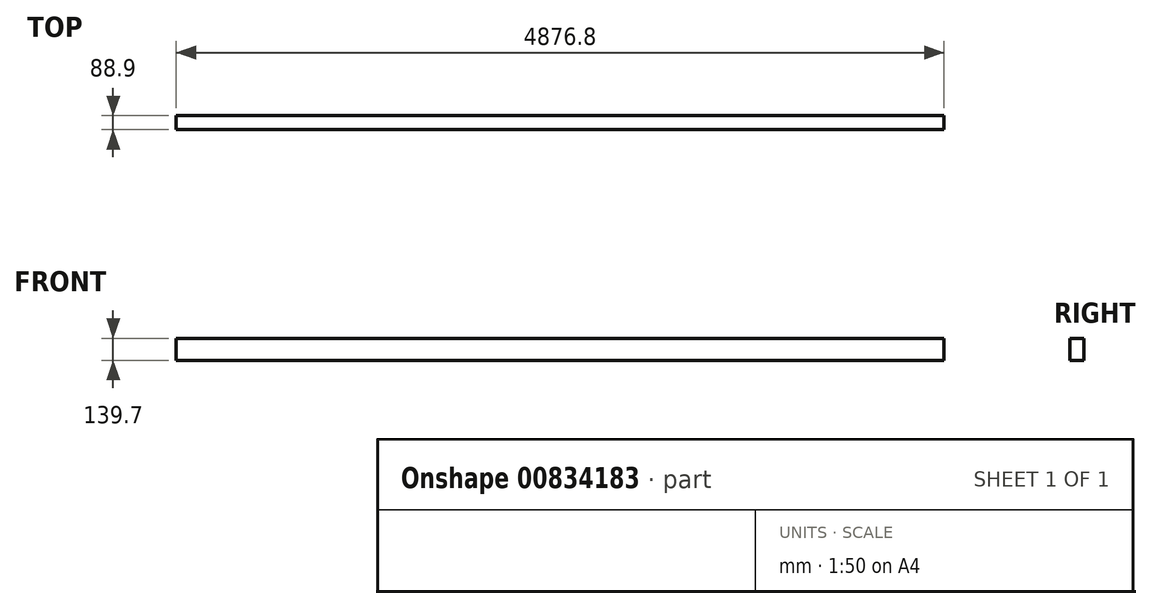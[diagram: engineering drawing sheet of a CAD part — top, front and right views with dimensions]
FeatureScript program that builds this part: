
annotation { "Feature Type Name" : "Feature", "Feature Type Description" : "" }
export const myFeature = defineFeature(function(context is Context, id is Id, definition is map)
    precondition{}
    {
        {
            var Q0;
            Q0=qCreatedBy(makeId("Right.planeOp"),FACE);
            var sketch = newSketch(context, id + "F0", { "sketchPlane" : qUnion([Q0])});
            skLineSegment(sketch, "E0.bottom", {"start": v(-44.45, -69.85) * mm, "end": v(44.45, -69.85) * mm});
            skLineSegment(sketch, "E0.top", {"start": v(-44.45, 69.85) * mm, "end": v(44.45, 69.85) * mm});
            skLineSegment(sketch, "E0.left", {"start": v(-44.45, -69.85) * mm, "end": v(-44.45, 69.85) * mm});
            skLineSegment(sketch, "E0.right", {"start": v(44.45, -69.85) * mm, "end": v(44.45, 69.85) * mm});
            skPoint(sketch, "E0.middle", {"position": v(0, 0) * mm});
            skSolve(sketch);
        }
        {
            var Q0;
            Q0=makeQuery(id+"F0.imprint","IMPRINT",FACE,{"disambiguationData":[TD([[makeQuery(id+"F0.imprint","IMPRINT",EDGE,{"derivedFrom":sQuery(id+"F0.wireOp",EDGE,"E0.bottom")}),1.0]])]});
            extrude(context, id + "F1", {"entities" : qUnion([Q0]), "depth" : 4876.8 * mm, "offsetDistance" : 25.4 * mm});
        }
    });
